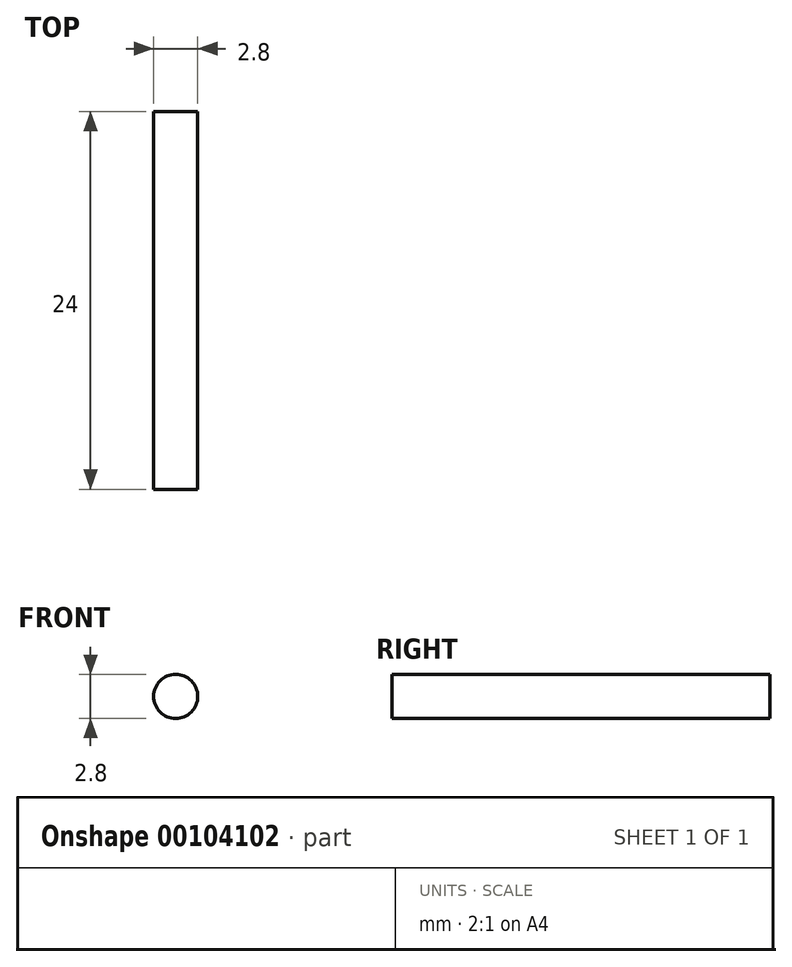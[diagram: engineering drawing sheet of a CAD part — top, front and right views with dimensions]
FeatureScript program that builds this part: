
annotation { "Feature Type Name" : "Feature", "Feature Type Description" : "" }
export const myFeature = defineFeature(function(context is Context, id is Id, definition is map)
    precondition{}
    {
        {
            var Q0;
            Q0=qCreatedBy(makeId("Front.planeOp"),FACE);
            var sketch = newSketch(context, id + "F0", { "sketchPlane" : qUnion([Q0])});
            skCircle(sketch, "E0", {"center": v(0, 0) * mm, "radius": 1.4 * mm});
            skSolve(sketch);
        }
        {
            var Q0;
            Q0 = qSketchRegion(id + "F0", true);
            extrude(context, id + "F1", {"entities" : qUnion([Q0]), "depth" : 24 * mm});
        }
    });
